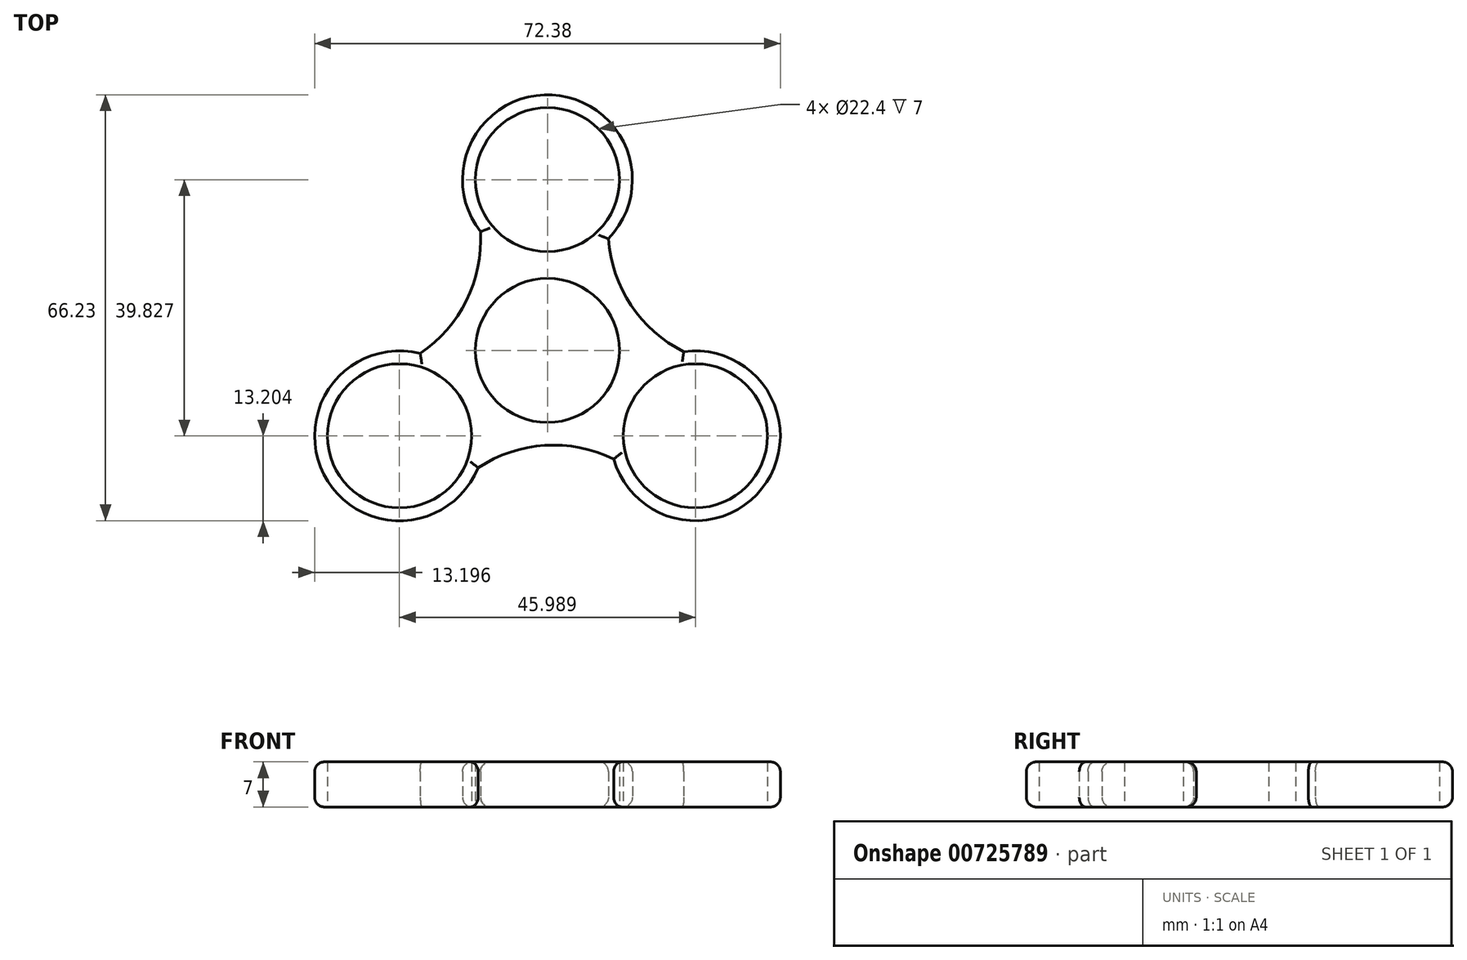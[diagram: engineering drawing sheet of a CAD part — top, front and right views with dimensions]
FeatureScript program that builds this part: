
annotation { "Feature Type Name" : "Feature", "Feature Type Description" : "" }
export const myFeature = defineFeature(function(context is Context, id is Id, definition is map)
    precondition{}
    {
        {
            var Q0;
            Q0=qCreatedBy(makeId("Top.planeOp"),FACE);
            var sketch = newSketch(context, id + "F0", { "sketchPlane" : qUnion([Q0])});
            skCircle(sketch, "E0", {"center": v(0, 0) * mm, "radius": 11.2 * mm});
            skCircle(sketch, "E1", {"center": v(0, 26.55) * mm, "radius": 11.2 * mm});
            skArc(sketch, "E2", {"start": v(9.48, 17.36) * mm, "mid": v(0.72, 39.73) * mm, "end": v(-10.42, 18.45) * mm});
            skArc(sketch, "E3.1.0", {"start": v(-19.78, -0.47) * mm, "mid": v(-34.77, -19.24) * mm, "end": v(-10.77, -18.25) * mm});
            skCircle(sketch, "E3.1.1", {"center": v(-23, -13.28) * mm, "radius": 11.2 * mm});
            skArc(sketch, "E3.2.0", {"start": v(10.3, -16.89) * mm, "mid": v(34.05, -20.49) * mm, "end": v(21.19, -0.2) * mm});
            skCircle(sketch, "E3.2.1", {"center": v(23, -13.28) * mm, "radius": 11.2 * mm});
            skArc(sketch, "E4", {"start": v(9.48, 17.36) * mm, "mid": v(13, 7.02) * mm, "end": v(21.19, -0.2) * mm});
            skArc(sketch, "E5.1.0", {"start": v(-19.78, -0.47) * mm, "mid": v(-12.58, 7.74) * mm, "end": v(-10.42, 18.45) * mm});
            skArc(sketch, "E5.2.0", {"start": v(10.3, -16.89) * mm, "mid": v(-0.42, -14.77) * mm, "end": v(-10.77, -18.25) * mm});
            skSolve(sketch);
        }
        {
            var Q0;
            Q0=makeQuery(id+"F0.imprint","IMPRINT",FACE,{"disambiguationData":[TD([[makeQuery(id+"F0.imprint","IMPRINT",EDGE,{"derivedFrom":sQuery(id+"F0.wireOp",EDGE,"E0")}),-1.0]])]});
            extrude(context, id + "F1", {"entities" : qUnion([Q0]), "depth" : 7 * mm, "offsetDistance" : 25 * mm});
        }
        {
            var Q0;
            Q0=makeQuery(id+"F1.opExtrude","CAP_EDGE",EDGE,{"disambiguationData":[OSD([sQuery(id+"F0.wireOp",EDGE,"E5.2.0")])],"isStart":false});
            var Q1;
            Q1=makeQuery(id+"F1.opExtrude","CAP_EDGE",EDGE,{"disambiguationData":[OSD([sQuery(id+"F0.wireOp",EDGE,"E4")])],"isStart":false});
            var Q2;
            Q2=makeQuery(id+"F1.opExtrude","CAP_EDGE",EDGE,{"disambiguationData":[OSD([sQuery(id+"F0.wireOp",EDGE,"E3.1.0")])],"isStart":false});
            var Q3;
            Q3=makeQuery(id+"F1.opExtrude","CAP_EDGE",EDGE,{"disambiguationData":[OSD([sQuery(id+"F0.wireOp",EDGE,"E5.1.0")])],"isStart":false});
            var Q4;
            Q4=makeQuery(id+"F1.opExtrude","CAP_EDGE",EDGE,{"disambiguationData":[OSD([sQuery(id+"F0.wireOp",EDGE,"E2")])],"isStart":false});
            var Q5;
            Q5=makeQuery(id+"F1.opExtrude","CAP_EDGE",EDGE,{"disambiguationData":[OSD([sQuery(id+"F0.wireOp",EDGE,"E3.2.0")])],"isStart":false});
            fillet(context, id + "F2", {"entities" : qUnion([Q0, Q1, Q2, Q3, Q4, Q5]), "radius" : 1.5 * mm, "tangentPropagation" : true, "allowEdgeOverflow" : false});
        }
        {
            var Q0;
            Q0=makeQuery(id+"F1.opExtrude","CAP_EDGE",EDGE,{"disambiguationData":[OSD([sQuery(id+"F0.wireOp",EDGE,"E3.2.0")])],"isStart":true});
            var Q1;
            Q1=makeQuery(id+"F1.opExtrude","CAP_EDGE",EDGE,{"disambiguationData":[OSD([sQuery(id+"F0.wireOp",EDGE,"E5.2.0")])],"isStart":true});
            var Q2;
            Q2=makeQuery(id+"F1.opExtrude","CAP_EDGE",EDGE,{"disambiguationData":[OSD([sQuery(id+"F0.wireOp",EDGE,"E3.1.0")])],"isStart":true});
            var Q3;
            Q3=makeQuery(id+"F1.opExtrude","CAP_EDGE",EDGE,{"disambiguationData":[OSD([sQuery(id+"F0.wireOp",EDGE,"E5.1.0")])],"isStart":true});
            var Q4;
            Q4=makeQuery(id+"F1.opExtrude","CAP_EDGE",EDGE,{"disambiguationData":[OSD([sQuery(id+"F0.wireOp",EDGE,"E2")])],"isStart":true});
            var Q5;
            Q5=makeQuery(id+"F1.opExtrude","CAP_EDGE",EDGE,{"disambiguationData":[OSD([sQuery(id+"F0.wireOp",EDGE,"E4")])],"isStart":true});
            fillet(context, id + "F3", {"entities" : qUnion([Q0, Q1, Q2, Q3, Q4, Q5]), "radius" : 1.5 * mm, "tangentPropagation" : true, "allowEdgeOverflow" : false});
        }
    });
